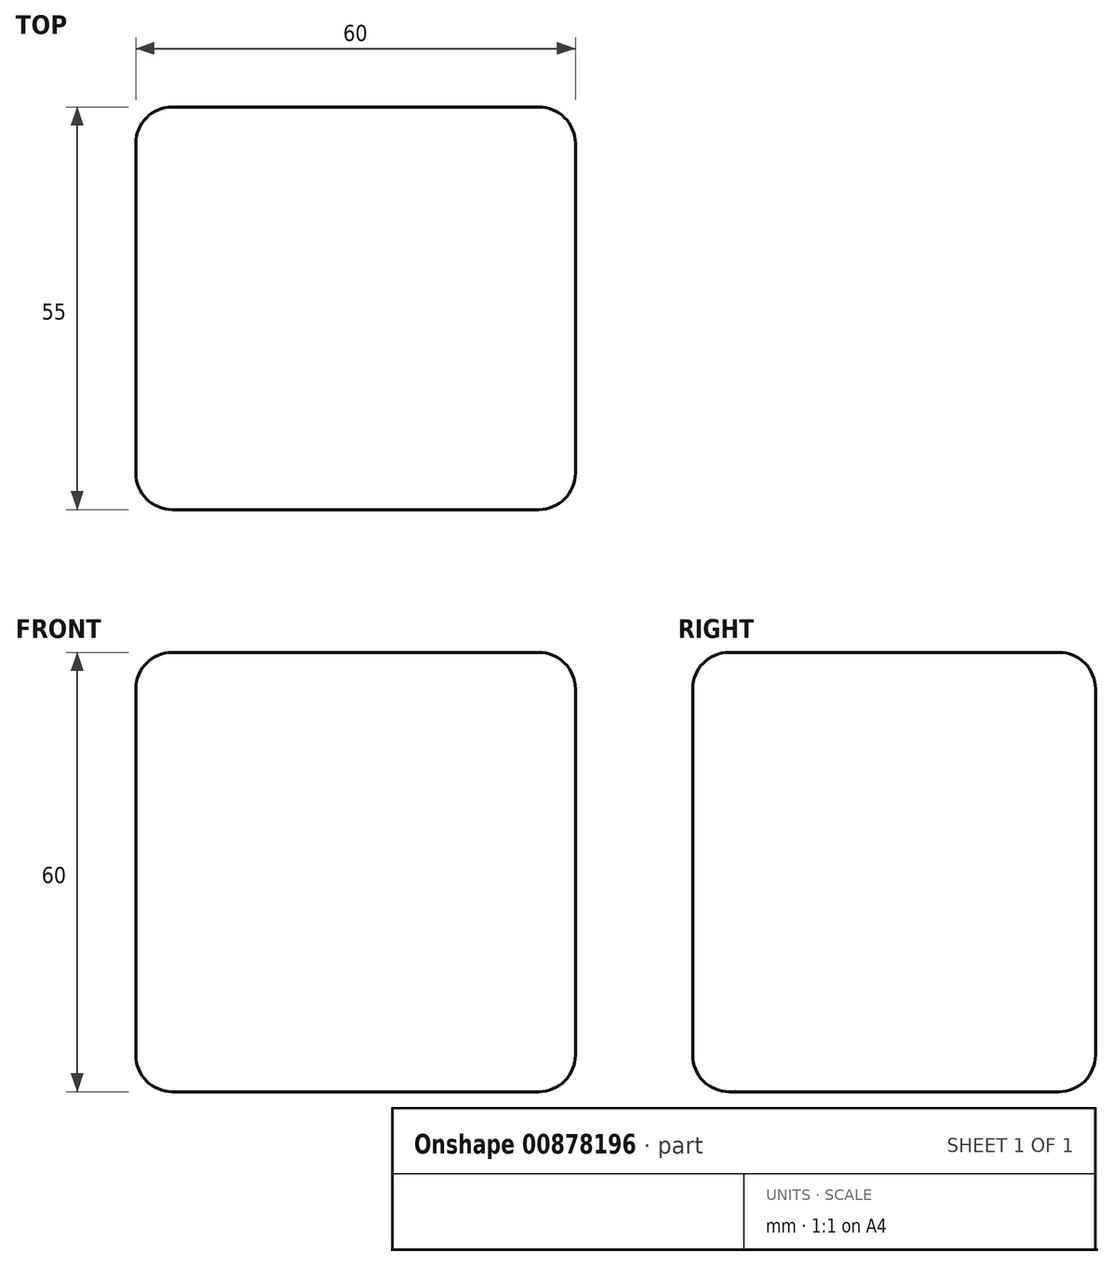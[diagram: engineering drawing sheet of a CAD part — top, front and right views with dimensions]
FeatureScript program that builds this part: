
annotation { "Feature Type Name" : "Feature", "Feature Type Description" : "" }
export const myFeature = defineFeature(function(context is Context, id is Id, definition is map)
    precondition{}
    {
        {
            var Q0;
            Q0=qCreatedBy(makeId("Front.planeOp"),FACE);
            var sketch = newSketch(context, id + "F0", { "sketchPlane" : qUnion([Q0])});
            skLineSegment(sketch, "E0.bottom", {"start": v(30, -30) * mm, "end": v(-30, -30) * mm});
            skLineSegment(sketch, "E0.top", {"start": v(30, 30) * mm, "end": v(-30, 30) * mm});
            skLineSegment(sketch, "E0.left", {"start": v(30, -30) * mm, "end": v(30, 30) * mm});
            skLineSegment(sketch, "E0.right", {"start": v(-30, -30) * mm, "end": v(-30, 30) * mm});
            skPoint(sketch, "E0.middle", {"position": v(0, 0) * mm});
            skSolve(sketch);
        }
        {
            var Q0;
            Q0 = qSketchRegion(id + "F0", true);
            extrude(context, id + "F1", {"entities" : qUnion([Q0]), "depth" : 30 * mm, "offsetDistance" : 25 * mm, "hasSecondDirection" : true, "secondDirectionOppositeDirection" : true, "secondDirectionDepth" : 25 * mm});
        }
        {
            var Q0;
            Q0=makeQuery(id+"F1.opExtrude","SWEPT_FACE",FACE,{"disambiguationData":[OSD([sQuery(id+"F0.wireOp",EDGE,"E0.top")])]});
            var Q1;
            Q1=makeQuery(id+"F1.opExtrude","SWEPT_FACE",FACE,{"disambiguationData":[OSD([sQuery(id+"F0.wireOp",EDGE,"E0.left")])]});
            var Q2;
            Q2=makeQuery(id+"F1.opExtrude","CAP_FACE",FACE,{"disambiguationData":[OSD([sQuery(id+"F0.wireOp",EDGE,"E0.bottom"),sQuery(id+"F0.wireOp",EDGE,"E0.top"),sQuery(id+"F0.wireOp",EDGE,"E0.left"),sQuery(id+"F0.wireOp",EDGE,"E0.right")])],"isStart":false});
            var Q3;
            Q3=makeQuery(id+"F1.opExtrude","CAP_FACE",FACE,{"disambiguationData":[OSD([sQuery(id+"F0.wireOp",EDGE,"E0.bottom"),sQuery(id+"F0.wireOp",EDGE,"E0.top"),sQuery(id+"F0.wireOp",EDGE,"E0.left"),sQuery(id+"F0.wireOp",EDGE,"E0.right")])],"isStart":true});
            var Q4;
            Q4=makeQuery(id+"F1.opExtrude","SWEPT_FACE",FACE,{"disambiguationData":[OSD([sQuery(id+"F0.wireOp",EDGE,"E0.bottom")])]});
            fillet(context, id + "F2", {"entities" : qUnion([Q0, Q1, Q2, Q3, Q4]), "radius" : 5 * mm, "tangentPropagation" : true, "allowEdgeOverflow" : false});
        }
    });
